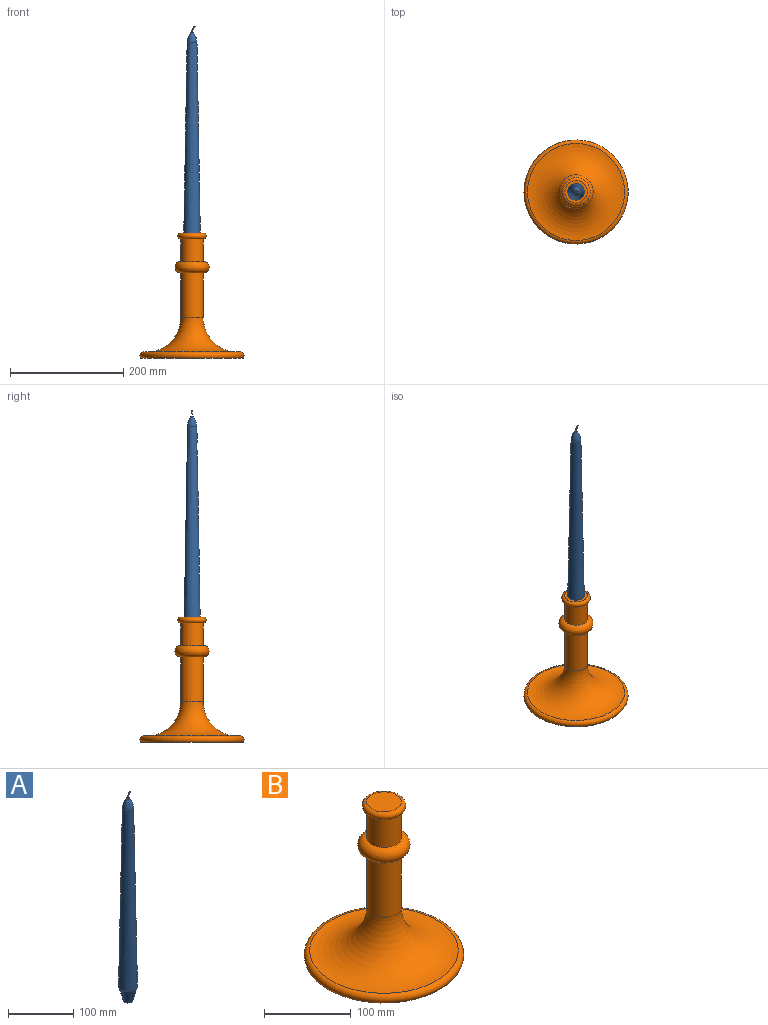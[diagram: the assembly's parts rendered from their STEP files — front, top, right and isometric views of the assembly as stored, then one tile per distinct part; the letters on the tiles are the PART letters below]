
ASSEMBLY  parts=2 mates=1
PART A: 7 faces, bbox 29.1x29.1x392.4 mm
  f0: plane 15x15mm, normal (0,0,-1), area 176.7mm2, adj f1
  f1: cone r=7.5mm half-angle=15deg, axis (0,0,1), area 1883.8mm2, adj f0,f2
  f2: cone r=14.54mm half-angle=1deg, axis (0,0,-1), area 24516mm2, adj f1,f3
  f3: revolved ~17.64x17.35mm, area 737.3mm2, adj f2,f4
  f4: plane 4x4mm, normal (0,0,1), area 10.8mm2, adj f3,f6
  f5: plane 1.5x1.09mm, normal (0.73,0,0.69), area 1.8mm2, adj f6
  f6: torus R=15mm, axis (0,1,0), area 57.6mm2, adj f4,f5
PART B: 8 faces, bbox 265.4x265.4x220.1 mm
  f0: torus R=20mm, axis (0,0,-1), area 2288.1mm2, adj f1,f7
  f1: plane 40x40mm, normal (0,0,1), area 1256.6mm2, adj f0
  f2: plane 180x180mm, normal (0,0,-1), area 25446.9mm2, adj f3
  f3: torus R=85.5mm, axis (0,0,-1), area 8268.9mm2, adj f2,f4
  f4: torus R=79.99mm, axis (0,0,-1), area 27732.6mm2, adj f3,f5
  f5: cylinder r=20mm len=78.77mm, axis (0,0,-1), area 9898mm2, adj f4,f6
  f6: torus R=20mm, axis (0,0,-1), area 5204.5mm2, adj f5,f7
  f7: cylinder r=20mm len=40mm, axis (0,0,-1), area 5026.5mm2, adj f0,f6
PLACE A t=(-25.99,73.21,216.05)mm
PLACE B t=(-25.99,73.21,22.32)mm fixed
MATE fastened A.f1 <-> B.f0  axis (0,0,-1) through (-25.99,73.21,242.32)mm
